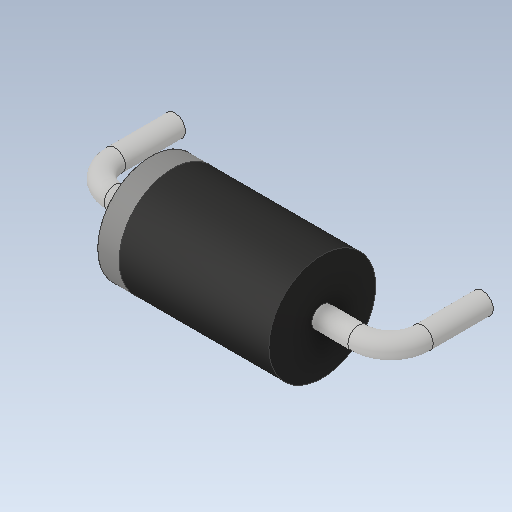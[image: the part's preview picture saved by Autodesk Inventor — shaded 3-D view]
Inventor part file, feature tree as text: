
AUTODESK INVENTOR PART (.ipt)
format: ipt  version: 2020 (Build 240168000, 168)  size: 126,464 bytes
history: imported  units: in
note: dims shown in document units (in); Inventor stores cm internally (conversion verified against a paired STEP export)
features: imported_body x1
ambient origin geometry x8: Origin, YZ Plane, XZ Plane, XY Plane, X Axis, Y Axis, Z Axis, Center Point
bodies: Solid1 (imported_parasolid), Body2 (imported_parasolid)
feature tree (1):
  imported_body  NMx_Import_Brep_tag  [imported B-rep: ~15 faces, bbox_mm=[15.28, 0.53, 4.57]]
